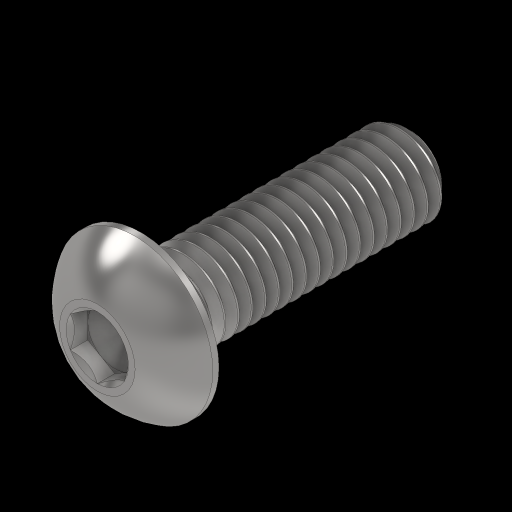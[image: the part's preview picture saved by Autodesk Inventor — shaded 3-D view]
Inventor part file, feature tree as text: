
AUTODESK INVENTOR PART (.ipt)
format: ipt  version: 2024.2 (Build 282272000, 272)  size: 653,824 bytes
history: native  units: in
note: dims shown in document units (in); Inventor stores cm internally (conversion verified against a paired STEP export)
features: revolve x1
ambient origin geometry x8: Origin, YZ Plane, XZ Plane, XY Plane, X Axis, Y Axis, Z Axis, Center Point
bodies: Solid1 (feature_tree)
feature tree (1):
  revolve  "Revolve2"  [1 undecoded]
note: 1 required parameter value undecoded (feature->parameter linkage not recoverable at this tier; creation-order binding heuristic only, values carry confidence <= 0.55)
